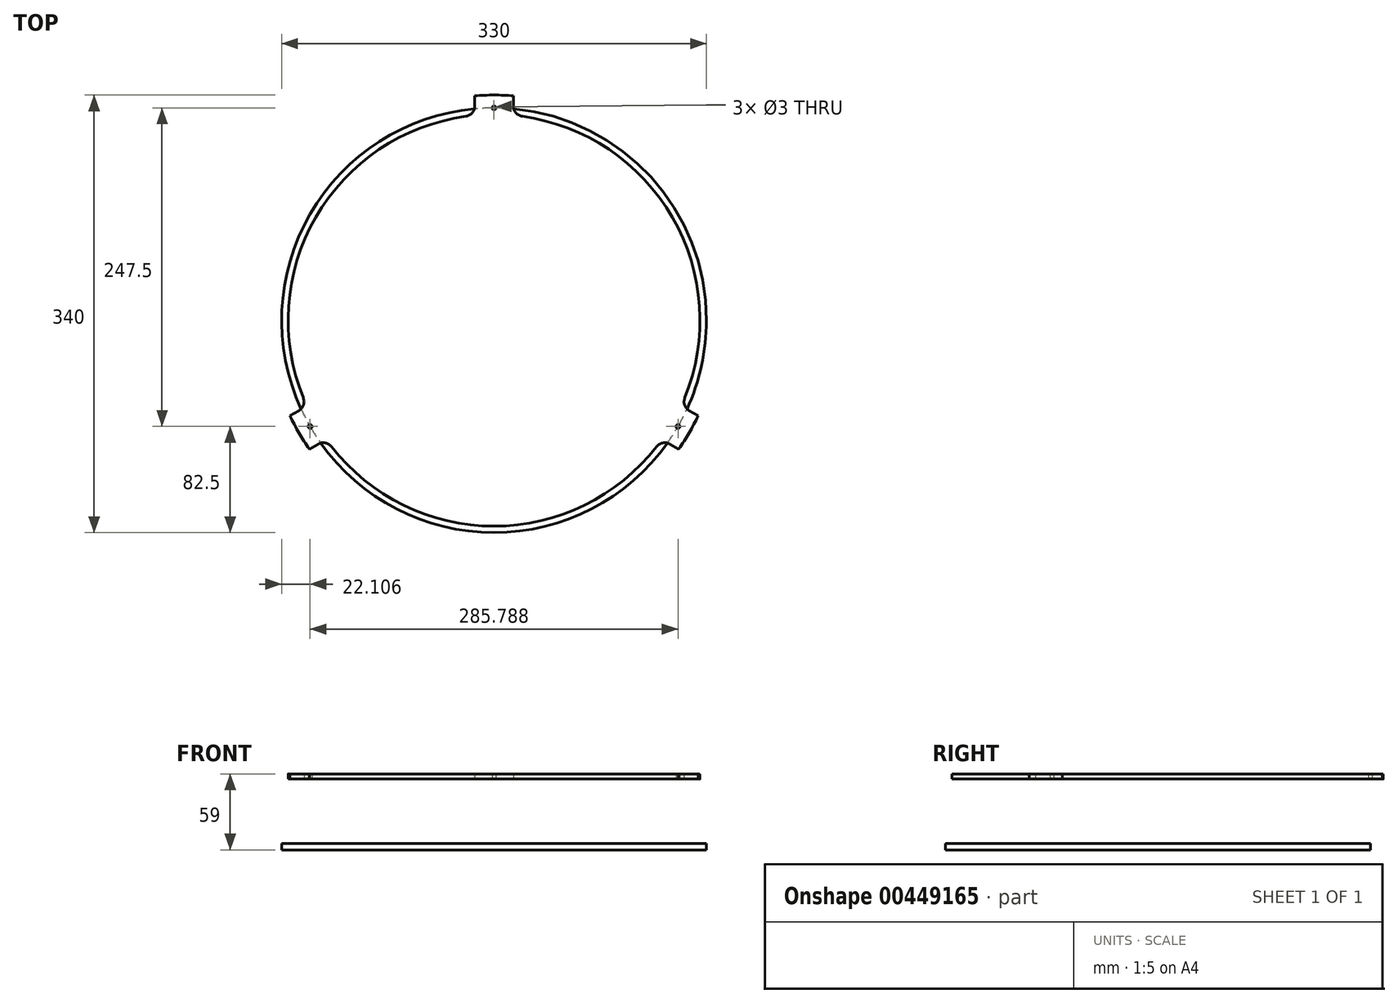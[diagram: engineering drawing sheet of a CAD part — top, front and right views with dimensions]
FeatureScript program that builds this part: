
annotation { "Feature Type Name" : "Feature", "Feature Type Description" : "" }
export const myFeature = defineFeature(function(context is Context, id is Id, definition is map)
    precondition{}
    {
        {
            var Q0;
            Q0=qCreatedBy(makeId("Top.planeOp"),FACE);
            var sketch = newSketch(context, id + "F0", { "sketchPlane" : qUnion([Q0])});
            skCircle(sketch, "E0", {"center": v(0, 0) * mm, "radius": 165 * mm});
            skSolve(sketch);
        }
        {
            var Q0;
            Q0=qSketchRegion(id+"F0",true);
            extrude(context, id + "F1", {"entities" : qUnion([Q0]), "depth" : 5 * mm});
        }
        {
            var Q0;
            Q0=makeQuery(id+"F1.opExtrude","CAP_FACE",FACE,{"disambiguationData":[OSD([sQuery(id+"F0.wireOp",EDGE,"E0")])],"isStart":false});
            cPlane(context, id + "F2", {"entities" : qUnion([Q0]), "cplaneType" : CPlaneType.OFFSET, "offset" : 50 * mm, "width" : 150 * mm, "height" : 150 * mm});
        }
        {
            var Q0;
            Q0=qCreatedBy(id+"F2.planeOp",FACE);
            var sketch = newSketch(context, id + "F3", { "sketchPlane" : qUnion([Q0])});
            skPoint(sketch, "E1.0", {"position": v(0, 0) * mm});
            skLineSegment(sketch, "E2", {"start": v(0, 0) * mm, "end": v(0, 165) * mm, "construction": true});
            skLineSegment(sketch, "E3", {"start": v(0, 0) * mm, "end": v(142.9, -82.5) * mm, "construction": true});
            skLineSegment(sketch, "E4", {"start": v(0, 0) * mm, "end": v(-142.9, -82.5) * mm, "construction": true});
            skArc(sketch, "E5", {"start": v(143.5, -100.17) * mm, "mid": v(151.55, -87.5) * mm, "end": v(158.5, -74.19) * mm});
            skCircle(sketch, "E6", {"center": v(-142.9, -82.5) * mm, "radius": 1.5 * mm});
            skCircle(sketch, "E7", {"center": v(0, 165) * mm, "radius": 1.5 * mm});
            skCircle(sketch, "E8", {"center": v(142.9, -82.5) * mm, "radius": 1.5 * mm});
            skCircle(sketch, "E9", {"center": v(0, 165) * mm, "radius": 4 * mm});
            skArc(sketch, "E10", {"start": v(-126.3, -98.22) * mm, "mid": v(0, -160) * mm, "end": v(126.3, -98.22) * mm});
            skLineSegment(sketch, "E11", {"start": v(-142.9, -82.5) * mm, "end": v(-151.55, -87.5) * mm, "construction": true});
            skLineSegment(sketch, "E12.0", {"start": v(-151.62, -70.22) * mm, "end": v(-158.5, -74.19) * mm});
            skLineSegment(sketch, "E13.MirrorCS", {"start": v(-136.62, -96.2) * mm, "end": v(-143.5, -100.17) * mm});
            skLineSegment(sketch, "E14", {"start": v(0, 165) * mm, "end": v(0, 175) * mm, "construction": true});
            skLineSegment(sketch, "E15.0", {"start": v(15, 166.42) * mm, "end": v(15, 174.36) * mm});
            skLineSegment(sketch, "E16.MirrorCS", {"start": v(-15, 166.42) * mm, "end": v(-15, 174.36) * mm});
            skLineSegment(sketch, "E17", {"start": v(142.9, -82.5) * mm, "end": v(151.55, -87.5) * mm, "construction": true});
            skLineSegment(sketch, "E18.0", {"start": v(136.62, -96.2) * mm, "end": v(143.5, -100.17) * mm});
            skLineSegment(sketch, "E19.MirrorCS", {"start": v(151.62, -70.22) * mm, "end": v(158.5, -74.19) * mm});
            skArc(sketch, "E20.trimOffspring", {"start": v(-158.5, -74.19) * mm, "mid": v(-151.55, -87.5) * mm, "end": v(-143.5, -100.17) * mm});
            skArc(sketch, "E21.trimOffspring", {"start": v(15, 174.36) * mm, "mid": v(0, 175) * mm, "end": v(-15, 174.36) * mm});
            skArc(sketch, "E22.trimOffspring", {"start": v(-21.9, 158.5) * mm, "mid": v(-138.56, 80) * mm, "end": v(-148.21, -60.28) * mm});
            skArc(sketch, "E23.trimOffspring", {"start": v(148.21, -60.28) * mm, "mid": v(138.56, 80) * mm, "end": v(21.9, 158.5) * mm});
            skPoint(sketch, "E24.visualSharp", {"position": v(-130.45, -92.64) * mm});
            skArc(sketch, "E24.filletArc", {"start": v(-126.3, -98.22) * mm, "mid": v(-131.09, -95.28) * mm, "end": v(-136.62, -96.2) * mm});
            skPoint(sketch, "E25.visualSharp", {"position": v(-145.45, -66.66) * mm});
            skArc(sketch, "E25.filletArc", {"start": v(-151.62, -70.22) * mm, "mid": v(-148.06, -65.89) * mm, "end": v(-148.21, -60.28) * mm});
            skPoint(sketch, "E26.visualSharp", {"position": v(130.45, -92.64) * mm});
            skArc(sketch, "E26.filletArc", {"start": v(136.62, -96.2) * mm, "mid": v(131.09, -95.28) * mm, "end": v(126.3, -98.22) * mm});
            skPoint(sketch, "E27.visualSharp", {"position": v(145.45, -66.66) * mm});
            skArc(sketch, "E27.filletArc", {"start": v(148.21, -60.28) * mm, "mid": v(148.06, -65.89) * mm, "end": v(151.62, -70.22) * mm});
            skPoint(sketch, "E28.visualSharp", {"position": v(15, 159.3) * mm});
            skArc(sketch, "E28.filletArc", {"start": v(15, 166.42) * mm, "mid": v(16.97, 161.16) * mm, "end": v(21.9, 158.5) * mm});
            skPoint(sketch, "E29.visualSharp", {"position": v(-15, 159.3) * mm});
            skArc(sketch, "E29.filletArc", {"start": v(-21.9, 158.5) * mm, "mid": v(-16.97, 161.16) * mm, "end": v(-15, 166.42) * mm});
            skSolve(sketch);
        }
        {
            var Q0;
            Q0=makeQuery(id+"F3.imprint","IMPRINT",FACE,{"disambiguationData":[TD([[makeQuery(id+"F3.imprint","IMPRINT",EDGE,{"derivedFrom":sQuery(id+"F3.wireOp",EDGE,"E5")}),1.0]])]});
            var Q1;
            Q1=makeQuery(id+"F3.imprint","IMPRINT",FACE,{"disambiguationData":[TD([[makeQuery(id+"F3.imprint","IMPRINT",EDGE,{"derivedFrom":sQuery(id+"F3.wireOp",EDGE,"E7")}),-1.0]])]});
            extrude(context, id + "F4", {"entities" : qUnion([Q0, Q1]), "depth" : 4 * mm});
        }
    });
